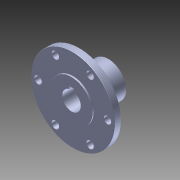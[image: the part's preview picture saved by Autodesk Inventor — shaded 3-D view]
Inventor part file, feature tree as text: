
AUTODESK INVENTOR PART (.ipt)
format: ipt  version: 2014 (Build 180170000, 170)  size: 156,672 bytes
history: native  units: in
note: dims shown in document units (in); Inventor stores cm internally (conversion verified against a paired STEP export)
features: other x2, chamfer x1
ambient origin geometry x8: Origin, YZ Plane, XZ Plane, XY Plane, X Axis, Y Axis, Z Axis, Center Point
bodies: Solid1 (feature_tree)
feature tree (3):
  other  "am-0077a-500 Key Hub r2.ipt"
  chamfer  "Chamfer2::am-0077a-500 Key Hub r2.ipt"  Distance=0.3937in
  other  "TaggingFeature1"
